# Revit family: EBRME-LED-228x-MPSx
name_source: partatom
category: Oprawy oświetleniowe
units: mm (PartAtom-declared; Revit-internal decimal feet)

## family parameters
Numer OmniClass = 23.80.70.11
Obiekt nadrzędny = Powierzchnia
Punkt obliczania pomieszczeń = Nie
Tnij formami wycięć po wczytaniu = Nie
Typ części = Normalny
Tytuł OmniClass = Luminaries for Internal Lighting
Współdzielony = Nie
Wymiar okrągłego złącza = Użyj średnicy
Źródło światła = Tak

## types (8) — shared parameters
Emituj kształt widoczny w renderingu = Nie
Emituj z długości prostokąta = 231 mm  [stored 0.757874 ft]
Emituj z szerokości prostokąta = 1135 mm  [stored 3.72375 ft]
Filtr koloru = 16777215
Kod zespołu = D5020200
Lampa = LED
Odchylenie kierunku = 90.00°
Plik sieci fotometrycznej = EBRE-LED 2285200-840 MPS.IES
Producent = RIDI Leuchten GmbH
URL = www.ridi.de
Zmiana temperatury barwowej przyciemniania lampy = <Brak>
brand = RIDI
conformity mark = CE
electrical safety class = 1
height = 60 mm  [stored 0.19685 ft]
ingress protection (IP) code = IP20
length = 1197 mm
nominal frequency = 50-60Hz
nominal voltage = 230
voltage type (AC, DC, UC) = AC
weight = 7.2 kg
width = 297 mm  [stored 0.974409 ft]
zero-valued in all types: Domyślna rzędna

## per-type parameters (varying)
| type | Model | Obciążenie pozorne | rated input power |
| EBRME-LED 228/2500-830 MPS | 0822891 | 16 VA | 16 |
| EBRME-LED 228/2500-830 MPS-DA | 0832891 | 16 VA | 16 |
| EBRME-LED 228/2700-840 MPS | 0822892 | 16 VA | 16 |
| EBRME-LED 228/2700-840 MPS-DA | 0832892 | 16 VA | 16 |
| EBRME-LED 228/5000-830 MPS | 0822893 | 32 VA | 32 |
| EBRME-LED 228/5000-830 MPS-DA | 0832893 | 32 VA | 32 |
| EBRME-LED 228/5200-840 MPS | 0822894 | 32 VA | 32 |
| EBRME-LED 228/5200-840 MPS-DA | 0832894 | 32 VA | 32 |

note: column(s) folded — value = type name in every type: product name

note: [stored X ft] marks values corroborated as IEEE doubles in the binary element streams (Revit-internal decimal feet)
